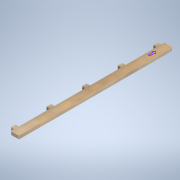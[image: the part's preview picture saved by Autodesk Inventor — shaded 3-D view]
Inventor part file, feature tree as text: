
AUTODESK INVENTOR PART (.ipt)
format: ipt  version: 2021 (Build 250183000, 183)  size: 165,376 bytes
history: native  units: mm
features: sketch x2, extrude x1
ambient origin geometry x8: Origin, YZ Plane, XZ Plane, XY Plane, X Axis, Y Axis, Z Axis, Center Point
bodies: Solid1 (feature_tree)
feature tree (3):
  extrude  "Extrusion1"  Depth=3.0mm
  sketch  "Sketch4"  dims[d36=4.0mm d46=90.0deg d50=50.0mm d52=31.75mm d53=10.0mm d55=10.0mm d57=2.9mm d11=0.5mm d12=0.872665mm d13=0.5mm d14=0.872665mm]
  sketch  "Sketch1"  dims[d4=3.0mm d5=0.0mm d35=3.0mm]
